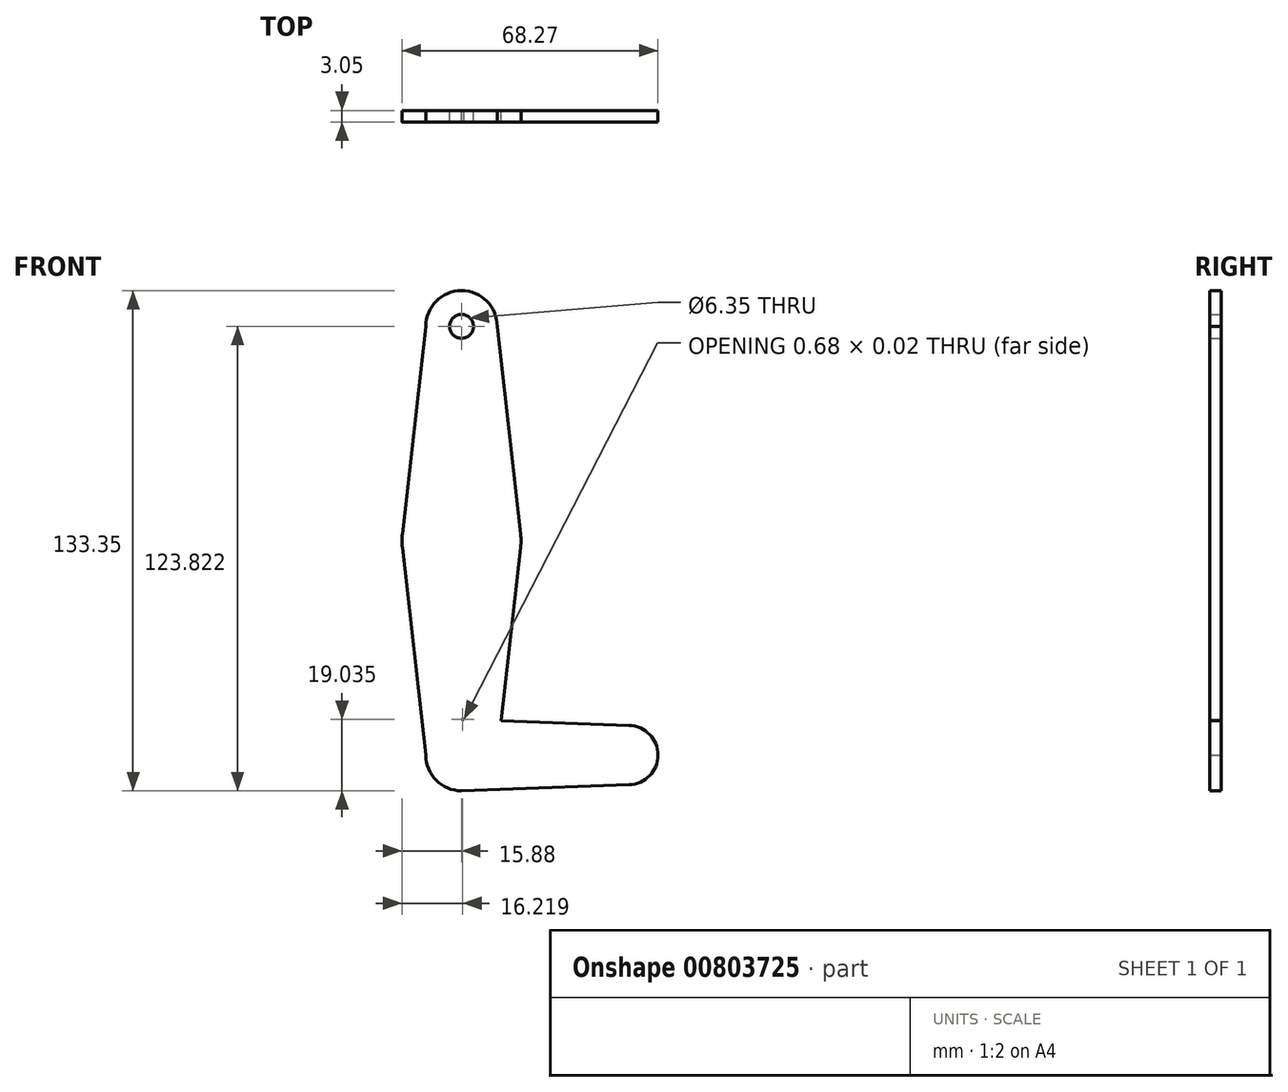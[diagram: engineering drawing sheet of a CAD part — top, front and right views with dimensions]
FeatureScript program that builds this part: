
annotation { "Feature Type Name" : "Feature", "Feature Type Description" : "" }
export const myFeature = defineFeature(function(context is Context, id is Id, definition is map)
    precondition{}
    {
        {
            var Q0;
            Q0=qCreatedBy(makeId("Front.planeOp"),FACE);
            var sketch = newSketch(context, id + "F0", { "sketchPlane" : qUnion([Q0])});
            skLineSegment(sketch, "E0", {"start": v(0, -210.73) * mm, "end": v(0, -325.03) * mm});
            skLineSegment(sketch, "E1", {"start": v(0, -325.03) * mm, "end": v(44.45, -325.03) * mm});
            skCircle(sketch, "E2", {"center": v(0, -210.73) * mm, "radius": 9.53 * mm});
            skPoint(sketch, "E3", {"position": v(0, -267.88) * mm});
            skCircle(sketch, "E4", {"center": v(0, -267.88) * mm, "radius": 15.88 * mm});
            skCircle(sketch, "E5", {"center": v(0, -325.03) * mm, "radius": 9.53 * mm});
            skCircle(sketch, "E6", {"center": v(44.45, -325.03) * mm, "radius": 7.94 * mm});
            skLineSegment(sketch, "E7", {"start": v(-9.52, -210.73) * mm, "end": v(-15.77, -266.1) * mm});
            skLineSegment(sketch, "E8", {"start": v(9.52, -210.73) * mm, "end": v(15.77, -266.1) * mm});
            skLineSegment(sketch, "E9", {"start": v(-15.78, -269.64) * mm, "end": v(-9.53, -325.03) * mm});
            skLineSegment(sketch, "E10", {"start": v(15.78, -269.64) * mm, "end": v(9.58, -325.03) * mm});
            skLineSegment(sketch, "E11", {"start": v(0, -315.5) * mm, "end": v(44.73, -317.1) * mm});
            skLineSegment(sketch, "E12", {"start": v(0, -334.55) * mm, "end": v(44.73, -332.96) * mm});
            skCircle(sketch, "E13", {"center": v(0, -210.73) * mm, "radius": 3.18 * mm});
            skSolve(sketch);
        }
        {
            var Q0;
            Q0=makeQuery(id+"F0.imprint","IMPRINT",FACE,{"disambiguationData":[TD([[makeQuery(id+"F0.imprint","IMPRINT",EDGE,{"derivedFrom":sQuery(id+"F0.wireOp",EDGE,"E13")}),-1.0]])]});
            var Q1;
            {var subQ5=sQuery(id+"F0.wireOp",EDGE,"E7");Q1=makeQuery(id+"F0.imprint","IMPRINT",FACE,{"disambiguationData":[TD([[makeQuery(id+"F0.imprint","IMPRINT",EDGE,{"derivedFrom":subQ5}),1.0]])]});}
            var Q2;
            {var subQ5=sQuery(id+"F0.wireOp",EDGE,"E9");Q2=makeQuery(id+"F0.imprint","IMPRINT",FACE,{"disambiguationData":[TD([[makeQuery(id+"F0.imprint","IMPRINT",EDGE,{"derivedFrom":subQ5}),1.0]])]});}
            var Q3;
            {var subQ0=sQuery(id+"F0.wireOp",EDGE,"E4");var subQ1=sQuery(id+"F0.wireOp",EDGE,"E0");var subQ2=makeQuery(id+"F0.imprint","INTERSECT",VERTEX,{"disambiguationData":[OD(0.0)],"derivedFrom":[subQ1,subQ0]});Q3=makeQuery(id+"F0.imprint","IMPRINT",FACE,{"disambiguationData":[TD([[makeQuery(id+"F0.imprint","IMPRINT",EDGE,{"disambiguationData":[TD([[subQ2,-1.0]])],"derivedFrom":subQ1}),-1.0]])]});}
            var Q4;
            {var subQ0=sQuery(id+"F0.wireOp",EDGE,"E4");var subQ1=sQuery(id+"F0.wireOp",EDGE,"E0");var subQ2=makeQuery(id+"F0.imprint","INTERSECT",VERTEX,{"disambiguationData":[OD(0.0)],"derivedFrom":[subQ1,subQ0]});Q4=makeQuery(id+"F0.imprint","IMPRINT",FACE,{"disambiguationData":[TD([[makeQuery(id+"F0.imprint","IMPRINT",EDGE,{"disambiguationData":[TD([[subQ2,-1.0]])],"derivedFrom":subQ1}),1.0]])]});}
            var Q5;
            {var subQ5=sQuery(id+"F0.wireOp",EDGE,"E8");Q5=makeQuery(id+"F0.imprint","IMPRINT",FACE,{"disambiguationData":[TD([[makeQuery(id+"F0.imprint","IMPRINT",EDGE,{"derivedFrom":subQ5}),-1.0]])]});}
            var Q6;
            {var subQ0=sQuery(id+"F0.wireOp",EDGE,"E10");var subQ1=sQuery(id+"F0.wireOp",EDGE,"E4");var subQ2=makeQuery(id+"F0.imprint","INTERSECT",VERTEX,{"derivedFrom":[subQ1,subQ0]});Q6=makeQuery(id+"F0.imprint","IMPRINT",FACE,{"disambiguationData":[TD([[makeQuery(id+"F0.imprint","IMPRINT",EDGE,{"disambiguationData":[TD([[subQ2,1.0]])],"derivedFrom":subQ1}),-1.0]])]});}
            var Q7;
            {var subQ4=sQuery(id+"F0.wireOp",EDGE,"E1");var subQ5=sQuery(id+"F0.wireOp",EDGE,"E0");var subQ6=makeQuery(id+"F0.imprint","INTERSECT",VERTEX,{"derivedFrom":[subQ5,subQ4]});Q7=makeQuery(id+"F0.imprint","IMPRINT",FACE,{"disambiguationData":[TD([[makeQuery(id+"F0.imprint","IMPRINT",EDGE,{"disambiguationData":[TD([[subQ6,-1.0]])],"derivedFrom":subQ4}),-1.0]])]});}
            var Q8;
            {var subQ0=sQuery(id+"F0.wireOp",EDGE,"E1");var subQ1=sQuery(id+"F0.wireOp",EDGE,"E0");var subQ2=makeQuery(id+"F0.imprint","INTERSECT",VERTEX,{"derivedFrom":[subQ1,subQ0]});Q8=makeQuery(id+"F0.imprint","IMPRINT",FACE,{"disambiguationData":[TD([[makeQuery(id+"F0.imprint","IMPRINT",EDGE,{"disambiguationData":[TD([[subQ2,-1.0]])],"derivedFrom":subQ0}),1.0]])]});}
            var Q9;
            {var subQ0=sQuery(id+"F0.wireOp",EDGE,"E10");var subQ1=sQuery(id+"F0.wireOp",EDGE,"E1");var subQ2=makeQuery(id+"F0.imprint","INTERSECT",VERTEX,{"derivedFrom":[subQ1,subQ0]});Q9=makeQuery(id+"F0.imprint","IMPRINT",FACE,{"disambiguationData":[TD([[makeQuery(id+"F0.imprint","IMPRINT",EDGE,{"disambiguationData":[TD([[subQ2,-1.0]])],"derivedFrom":subQ1}),1.0]])]});}
            var Q10;
            {var subQ0=sQuery(id+"F0.wireOp",EDGE,"E10");var subQ1=sQuery(id+"F0.wireOp",EDGE,"E1");var subQ2=makeQuery(id+"F0.imprint","INTERSECT",VERTEX,{"derivedFrom":[subQ1,subQ0]});Q10=makeQuery(id+"F0.imprint","IMPRINT",FACE,{"disambiguationData":[TD([[makeQuery(id+"F0.imprint","IMPRINT",EDGE,{"disambiguationData":[TD([[subQ2,1.0]])],"derivedFrom":subQ1}),1.0]])]});}
            var Q11;
            {var subQ3=sQuery(id+"F0.wireOp",EDGE,"E1");var subQ8=makeQuery(id+"F0.imprint","INTERSECT",VERTEX,{"derivedFrom":[subQ3,sQuery(id+"F0.wireOp",EDGE,"E10")]});Q11=makeQuery(id+"F0.imprint","IMPRINT",FACE,{"disambiguationData":[TD([[makeQuery(id+"F0.imprint","IMPRINT",EDGE,{"disambiguationData":[TD([[subQ8,1.0]])],"derivedFrom":subQ3}),-1.0]])]});}
            var Q12;
            {var subQ0=sQuery(id+"F0.wireOp",EDGE,"E6");var subQ1=makeQuery(id+"F0.imprint","INTERSECT",VERTEX,{"derivedFrom":[subQ0,sQuery(id+"F0.wireOp",EDGE,"E11")]});Q12=makeQuery(id+"F0.imprint","IMPRINT",FACE,{"disambiguationData":[TD([[makeQuery(id+"F0.imprint","IMPRINT",EDGE,{"disambiguationData":[TD([[subQ1,-1.0]])],"derivedFrom":subQ0}),1.0]])]});}
            extrude(context, id + "F1", {"entities" : qUnion([Q0, Q1, Q2, Q3, Q4, Q5, Q6, Q7, Q8, Q9, Q10, Q11, Q12]), "depth" : 3.05 * mm, "offsetDistance" : 25.4 * mm});
        }
    });
